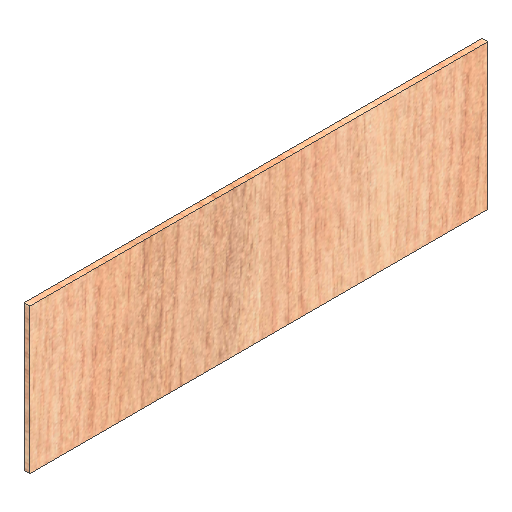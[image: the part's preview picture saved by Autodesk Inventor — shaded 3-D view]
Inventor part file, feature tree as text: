
AUTODESK INVENTOR PART (.ipt)
format: ipt  version: 2021 (Build 250183000, 183)  size: 276,992 bytes
history: native  units: mm
features: extrude x1, sketch x1
ambient origin geometry x8: Origin, YZ Plane, XZ Plane, XY Plane, X Axis, Y Axis, Z Axis, Center Point
bodies: Solid1 (feature_tree)
feature tree (2):
  extrude  "Extrusion1"  Depth=315.73mm
  sketch  "Sketch1"  dims[d0=100.0mm d1=315.73mm d2=4.0mm d3=0.0mm]
